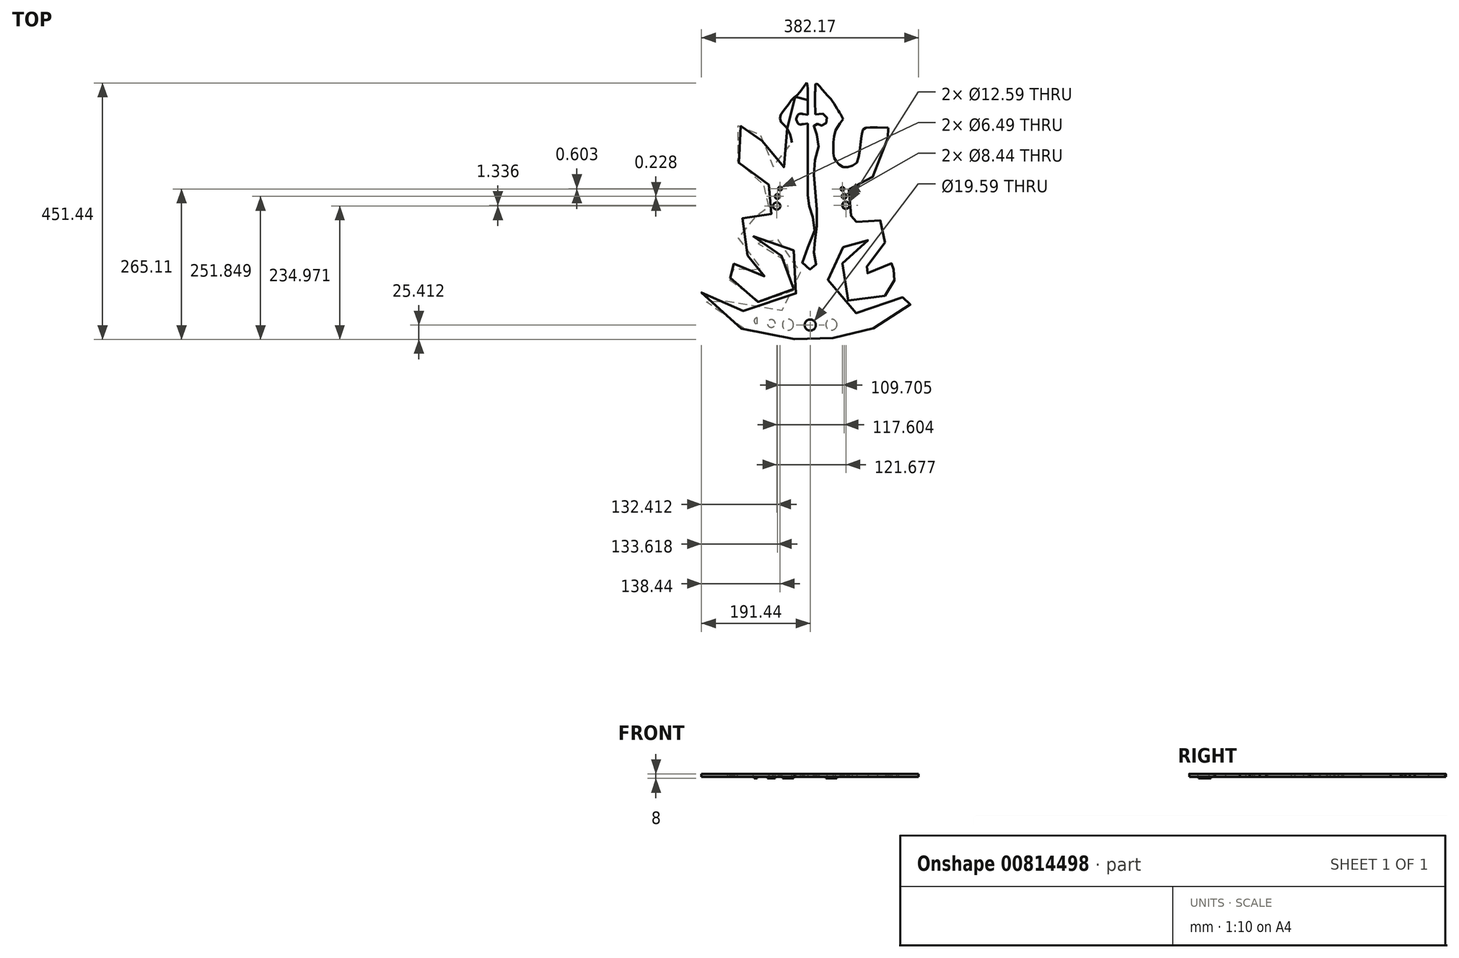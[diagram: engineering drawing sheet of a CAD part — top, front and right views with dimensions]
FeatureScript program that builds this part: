
annotation { "Feature Type Name" : "Feature", "Feature Type Description" : "" }
export const myFeature = defineFeature(function(context is Context, id is Id, definition is map)
    precondition{}
    {
        {
            var Q0;
            Q0=qCreatedBy(makeId("Top.planeOp"),FACE);
            var sketch = newSketch(context, id + "F0", { "sketchPlane" : qUnion([Q0])});
            skLineSegment(sketch, "E0", {"start": v(-4.07, 197.26) * mm, "end": v(-4.07, 171.34) * mm});
            skLineSegment(sketch, "E1", {"start": v(-4.07, 171.34) * mm, "end": v(-12.14, 172.64) * mm});
            skFitSpline(sketch, "E2", {"points": [v(-27.78, -223.43) * mm, v(-42.94, -221.77) * mm, v(-69.34, -218.88) * mm, v(-104.97, -210.79) * mm, v(-135.5, -198.39) * mm, v(-162.45, -178.55) * mm, v(-179.85, -161.54) * mm, v(-191.21, -140.43) * mm, v(-181.78, -135.12) * mm, v(-173.9, -139.63) * mm, v(-153.47, -153.55) * mm, v(-119.58, -173.02) * mm, v(-72.5, -180.75) * mm, v(-39.69, -165.64) * mm, v(-25.84, -144.71) * mm, v(-19.36, -127) * mm, v(-17.26, -107.43) * mm, v(-18.85, -88.24) * mm, v(-26.88, -70.7) * mm, v(-42.32, -56.3) * mm, v(-63.48, -45.68) * mm, v(-80.48, -39.04) * mm, v(-99.52, -40.32) * mm, v(-97.55, -50) * mm, v(-92.42, -54.8) * mm, v(-83.47, -58.4) * mm, v(-71.63, -62.83) * mm, v(-59.15, -70.9) * mm, v(-46.77, -80.5) * mm, v(-37.64, -92.94) * mm, v(-30.85, -106.86) * mm, v(-28.35, -119.67) * mm, v(-27.45, -129.59) * mm, v(-29.76, -137.09) * mm, v(-35.9, -144.2) * mm, v(-45.6, -151.88) * mm, v(-59.67, -157.06) * mm, v(-80.04, -159.95) * mm, v(-105.82, -152.76) * mm, v(-128.56, -141.2) * mm, v(-144.7, -127.23) * mm, v(-143.77, -118.69) * mm, v(-142.48, -116.34) * mm, v(-140.4, -115.67) * mm, v(-138.04, -115.96) * mm, v(-137.78, -113.15) * mm, v(-139.93, -110.3) * mm, v(-141.37, -105.83) * mm, v(-140.18, -100.45) * mm, v(-136.5, -99.2) * mm, v(-133.43, -99.09) * mm, v(-132.67, -96.28) * mm, v(-133.67, -92.96) * mm, v(-134.96, -86.24) * mm, v(-125.27, -87.3) * mm, v(-116.17, -95.98) * mm, v(-98.06, -103.5) * mm, v(-87, -112.38) * mm, v(-71.72, -109.66) * mm, v(-75.02, -105.8) * mm, v(-77.34, -103.91) * mm, v(-84.68, -99.95) * mm, v(-96.09, -91.59) * mm, v(-109.3, -77.45) * mm, v(-120.5, -61.9) * mm, v(-126.28, -45.64) * mm, v(-128.12, -31.2) * mm, v(-126.19, -17.15) * mm, v(-113.92, -8.45) * mm, v(-97.91, -6.5) * mm, v(-83.24, -8) * mm, v(-72.65, -14.15) * mm, v(-65.12, -8.82) * mm, v(-70.22, -0.24) * mm, v(-72.66, 8.71) * mm, v(-72.74, 20.19) * mm, v(-69.7, 30.44) * mm, v(-66.22, 39.17) * mm, v(-69.23, 47.47) * mm, v(-78.48, 47.54) * mm, v(-88.89, 50.35) * mm, v(-100.81, 57) * mm, v(-113.16, 67.16) * mm, v(-123.18, 81.99) * mm, v(-131.46, 100.93) * mm, v(-134, 120.7) * mm, v(-139.55, 138.3) * mm, v(-128.76, 152.03) * mm, v(-114.95, 149.55) * mm, v(-103.32, 150.04) * mm, v(-96.62, 149.3) * mm, v(-90.65, 148.51) * mm, v(-89.41, 141.65) * mm, v(-86.78, 133.64) * mm, v(-83.73, 118.01) * mm, v(-80.5, 101.92) * mm, v(-74.75, 85.75) * mm, v(-62.71, 79.55) * mm, v(-48.22, 78.44) * mm, v(-35.8, 91.84) * mm, v(-32.91, 108.6) * mm, v(-32.69, 125.44) * mm, v(-37.13, 140.3) * mm, v(-44.1, 152.06) * mm, v(-52.65, 161.04) * mm, v(-51.16, 173.08) * mm, v(-42.39, 184.23) * mm, v(-30.13, 200.74) * mm, v(-19.64, 208.94) * mm, v(-6.48, 227.3) * mm, v(-4.56, 217.3) * mm, v(-4.29, 209.32) * mm, v(-4.15, 201.7) * mm, v(-4.07, 197.26) * mm]});
            skLineSegment(sketch, "E3", {"start": v(-12.14, 155.2) * mm, "end": v(-4.07, 156.51) * mm});
            skLineSegment(sketch, "E4", {"start": v(-4.07, 156.51) * mm, "end": v(-4.07, 30.08) * mm});
            skFitSpline(sketch, "E5", {"points": [v(-12.14, 172.64) * mm, v(-13.86, 172.95) * mm, v(-16.72, 173.45) * mm, v(-20.98, 172.24) * mm, v(-22.95, 168.98) * mm, v(-24.42, 165.75) * mm, v(-24.42, 162.1) * mm, v(-22.95, 158.87) * mm, v(-20.98, 155.6) * mm, v(-16.72, 154.4) * mm, v(-13.86, 154.9) * mm, v(-12.14, 155.2) * mm]});
            skLineSegment(sketch, "E6", {"start": v(15.66, 173) * mm, "end": v(9.05, 172.22) * mm});
            skLineSegment(sketch, "E7", {"start": v(9.05, 172.22) * mm, "end": v(8.5, 196.44) * mm});
            skFitSpline(sketch, "E8", {"points": [v(-4.07, 30.08) * mm, v(0.64, 2.36) * mm, v(7.04, -35.24) * mm, v(-12.93, -93.82) * mm, v(8.43, -98.54) * mm, v(6.9, -73.98) * mm, v(10.46, -38.3) * mm, v(10.12, 24.62) * mm, v(7.47, 86.7) * mm, v(14.74, 126.78) * mm, v(6.06, 150.58) * mm, v(10.96, 156.05) * mm, v(12.9, 155.35) * mm, v(16, 153.85) * mm, v(21.44, 152.49) * mm, v(27.59, 156.03) * mm, v(29.76, 162.49) * mm, v(28.16, 168.96) * mm, v(22.57, 173.23) * mm, v(18.1, 173.08) * mm, v(15.66, 173) * mm]});
            skLineSegment(sketch, "E9", {"start": v(53.13, 172.82) * mm, "end": v(57.73, 163.81) * mm});
            skLineSegment(sketch, "E10", {"start": v(57.73, 163.81) * mm, "end": v(51.96, 156.16) * mm});
            skFitSpline(sketch, "E11", {"points": [v(8.5, 196.44) * mm, v(8.48, 200.64) * mm, v(8.43, 207.95) * mm, v(8.72, 215.84) * mm, v(10.22, 226.22) * mm, v(27.3, 208.98) * mm, v(38.21, 196.83) * mm, v(48.1, 180.91) * mm, v(53.13, 172.82) * mm]});
            skLineSegment(sketch, "E12", {"start": v(118, 149.2) * mm, "end": v(137, 148.51) * mm});
            skLineSegment(sketch, "E13", {"start": v(137, 148.51) * mm, "end": v(136.6, 130.73) * mm});
            skFitSpline(sketch, "E14", {"points": [v(51.96, 156.16) * mm, v(49.65, 152.5) * mm, v(44.74, 144.7) * mm, v(41.51, 129.6) * mm, v(40.88, 115.06) * mm, v(41.03, 103) * mm, v(42.36, 94.86) * mm, v(46.59, 88.17) * mm, v(52.62, 82.2) * mm, v(61.87, 79.03) * mm, v(71.4, 80.56) * mm, v(81.27, 86.3) * mm, v(86.1, 101.43) * mm, v(87.95, 117.39) * mm, v(89.9, 132.44) * mm, v(91.71, 141.38) * mm, v(94.53, 147.33) * mm, v(100.44, 148.82) * mm, v(108.05, 149.43) * mm, v(114.31, 149.28) * mm, v(118, 149.2) * mm]});
            skLineSegment(sketch, "E15", {"start": v(-27.78, -223.43) * mm, "end": v(-27.78, -223.43) * mm});
            skFitSpline(sketch, "E16", {"points": [v(136.6, 130.73) * mm, v(134.72, 117.75) * mm, v(131.09, 92.65) * mm, v(109.62, 61.76) * mm, v(86.9, 50.24) * mm, v(73.37, 47.56) * mm, v(70.04, 46.2) * mm, v(67.28, 44.07) * mm, v(67.98, 39.93) * mm, v(68.66, 34.92) * mm, v(71.23, 25.92) * mm, v(74.1, 14.75) * mm, v(74.04, 0.98) * mm, v(70.44, -8.65) * mm, v(67.55, -15.7) * mm, v(66.47, -19.1) * mm, v(66.49, -22.73) * mm, v(70.32, -21.7) * mm, v(73.97, -20.63) * mm, v(79.68, -17.9) * mm, v(86.79, -15.27) * mm, v(95.24, -13.2) * mm, v(104.7, -12) * mm, v(113.21, -11) * mm, v(121.49, -12.96) * mm, v(126.38, -18.58) * mm, v(132.04, -23.5) * mm, v(133.96, -31.95) * mm, v(132.86, -40.83) * mm, v(131.83, -50.54) * mm, v(129.4, -59.13) * mm, v(124.8, -68.94) * mm, v(115.72, -79.87) * mm, v(103.93, -92.1) * mm, v(93.6, -100.17) * mm, v(86.96, -104.93) * mm, v(84.8, -106.96) * mm, v(82.54, -110.6) * mm, v(93.53, -111.43) * mm, v(102.94, -106.41) * mm, v(117.74, -100.94) * mm, v(129.33, -94.52) * mm, v(136.23, -92.35) * mm, v(140.93, -88.8) * mm, v(143.94, -92.13) * mm, v(141.44, -96.46) * mm, v(138.85, -100.35) * mm, v(133.29, -104.15) * mm, v(137.44, -108.85) * mm, v(142.5, -104.71) * mm, v(148.88, -100.28) * mm, v(152.53, -107.9) * mm, v(146.96, -113.72) * mm, v(141.76, -117.65) * mm, v(142.21, -124.34) * mm, v(147.9, -120.35) * mm, v(152.15, -117.65) * mm, v(155.87, -122) * mm, v(152.5, -129.64) * mm, v(144.33, -138.59) * mm, v(130.25, -147.93) * mm, v(111.68, -156.34) * mm, v(90.6, -159.74) * mm, v(69.55, -156.71) * mm, v(50.9, -144.4) * mm, v(45, -118.03) * mm, v(57.52, -89.31) * mm, v(78.11, -70.27) * mm, v(93.37, -59.83) * mm, v(101.85, -53.6) * mm, v(100.28, -46.98) * mm, v(94.27, -44.13) * mm, v(85.45, -46.21) * mm, v(73.7, -51.09) * mm, v(59.8, -59.9) * mm, v(47, -71.52) * mm, v(34.4, -87.22) * mm, v(30.25, -110.58) * mm, v(35.13, -136.65) * mm, v(50.44, -162.28) * mm, v(81.3, -177.61) * mm, v(121.17, -173.42) * mm, v(153.55, -155.2) * mm, v(172.05, -143.18) * mm, v(185.83, -135.03) * mm, v(190.31, -148.68) * mm, v(175.16, -163.56) * mm, v(156.15, -182.25) * mm, v(130.34, -197.3) * mm, v(104.67, -206.44) * mm, v(81.91, -213.55) * mm, v(57.48, -219.65) * mm, v(29.45, -222.08) * mm, v(0.4, -224.1) * mm, v(-19.38, -223.63) * mm, v(-27.78, -223.43) * mm]});
            skSolve(sketch);
        }
        {
            var Q0;
            Q0=makeQuery(id+"F0.imprint","IMPRINT",FACE,{"disambiguationData":[TD([[makeQuery(id+"F0.imprint","IMPRINT",EDGE,{"derivedFrom":sQuery(id+"F0.wireOp",EDGE,"E0")}),-1.0]])]});
            var sketch = newSketch(context, id + "F1", { "sketchPlane" : qUnion([Q0])});
            skSolve(sketch);
        }
        {
            var Q0;
            Q0=makeQuery(id+"F1.imprint","IMPRINT",FACE,{"disambiguationData":[TD([[makeQuery(id+"F1.imprint","IMPRINT",EDGE,{"derivedFrom":makeQuery(id+"F0.imprint","IMPRINT",EDGE,{"derivedFrom":sQuery(id+"F0.wireOp",EDGE,"E0")})}),-1.0]])]});
            extrude(context, id + "F2", {"entities" : qUnion([Q0]), "depth" : 5 * mm, "offsetDistance" : 25 * mm});
        }
        {
            var Q0;
            Q0=makeQuery(id+"F2.opExtrude","CAP_FACE",FACE,{"disambiguationData":[OSD([sQuery(id+"F0.wireOp",EDGE,"E0"),sQuery(id+"F0.wireOp",EDGE,"E1"),sQuery(id+"F0.wireOp",EDGE,"E2"),sQuery(id+"F0.wireOp",EDGE,"E3"),sQuery(id+"F0.wireOp",EDGE,"E4"),sQuery(id+"F0.wireOp",EDGE,"E5"),sQuery(id+"F0.wireOp",EDGE,"E6"),sQuery(id+"F0.wireOp",EDGE,"E7"),sQuery(id+"F0.wireOp",EDGE,"E8"),sQuery(id+"F0.wireOp",EDGE,"E9"),sQuery(id+"F0.wireOp",EDGE,"E10"),sQuery(id+"F0.wireOp",EDGE,"E11"),sQuery(id+"F0.wireOp",EDGE,"E12"),sQuery(id+"F0.wireOp",EDGE,"E13"),sQuery(id+"F0.wireOp",EDGE,"E14"),sQuery(id+"F0.wireOp",EDGE,"E15"),sQuery(id+"F0.wireOp",EDGE,"E16")])],"isStart":false});
            var sketch = newSketch(context, id + "F3", { "sketchPlane" : qUnion([Q0])});
            skCircle(sketch, "E17", {"center": v(0, -198.73) * mm, "radius": 9.8 * mm});
            skSolve(sketch);
        }
        {
            var Q0;
            Q0 = qSketchRegion(id + "F3", true);
            var Q1;
            Q1 = qSketchRegion(id + "F5", true);
            extrude(context, id + "F4", {"entities" : qUnion([Q0, Q1]), "operationType" : NewBodyOperationType.REMOVE, "oppositeDirection" : true, "depth" : 25 * mm, "offsetDistance" : 25 * mm});
        }
        {
            var Q0;
            Q0=makeQuery(id+"F0.imprint","IMPRINT",FACE,{"disambiguationData":[TD([[makeQuery(id+"F0.imprint","IMPRINT",EDGE,{"derivedFrom":sQuery(id+"F0.wireOp",EDGE,"E0")}),-1.0]])]});
            var sketch = newSketch(context, id + "F5", { "sketchPlane" : qUnion([Q0])});
            skCircle(sketch, "E18", {"center": v(-59.03, 10.83) * mm, "radius": 6.3 * mm});
            skCircle(sketch, "E19", {"center": v(-57.82, 27.7) * mm, "radius": 4.22 * mm});
            skCircle(sketch, "E20", {"center": v(-53, 41.57) * mm, "radius": 3.25 * mm});
            skCircle(sketch, "E21", {"center": v(62.65, 12.17) * mm, "radius": 6.3 * mm});
            skCircle(sketch, "E22", {"center": v(59.78, 27.94) * mm, "radius": 4.22 * mm});
            skCircle(sketch, "E23", {"center": v(56.7, 40.97) * mm, "radius": 3.25 * mm});
            skSolve(sketch);
        }
        {
            var Q0;
            Q0=makeQuery(id+"F5.imprint","IMPRINT",FACE,{"disambiguationData":[TD([[makeQuery(id+"F5.imprint","IMPRINT",EDGE,{"derivedFrom":sQuery(id+"F5.wireOp",EDGE,"E21")}),1.0]])]});
            var Q1;
            Q1=makeQuery(id+"F5.imprint","IMPRINT",FACE,{"disambiguationData":[TD([[makeQuery(id+"F5.imprint","IMPRINT",EDGE,{"derivedFrom":sQuery(id+"F5.wireOp",EDGE,"E18")}),1.0]])]});
            var Q2;
            Q2=makeQuery(id+"F5.imprint","IMPRINT",FACE,{"disambiguationData":[TD([[makeQuery(id+"F5.imprint","IMPRINT",EDGE,{"derivedFrom":sQuery(id+"F5.wireOp",EDGE,"E20")}),1.0]])]});
            var Q3;
            Q3=makeQuery(id+"F5.imprint","IMPRINT",FACE,{"disambiguationData":[TD([[makeQuery(id+"F5.imprint","IMPRINT",EDGE,{"derivedFrom":sQuery(id+"F5.wireOp",EDGE,"E22")}),1.0]])]});
            var Q4;
            Q4=makeQuery(id+"F5.imprint","IMPRINT",FACE,{"disambiguationData":[TD([[makeQuery(id+"F5.imprint","IMPRINT",EDGE,{"derivedFrom":sQuery(id+"F5.wireOp",EDGE,"E19")}),1.0]])]});
            var Q5;
            Q5=makeQuery(id+"F5.imprint","IMPRINT",FACE,{"disambiguationData":[TD([[makeQuery(id+"F5.imprint","IMPRINT",EDGE,{"derivedFrom":sQuery(id+"F5.wireOp",EDGE,"E23")}),1.0]])]});
            extrude(context, id + "F6", {"entities" : qUnion([Q0, Q1, Q2, Q3, Q4, Q5]), "operationType" : NewBodyOperationType.REMOVE, "depth" : 5 * mm, "offsetDistance" : 25 * mm});
        }
        {
            var Q0;
            Q0=makeQuery(id+"F0.imprint","IMPRINT",FACE,{"disambiguationData":[TD([[makeQuery(id+"F0.imprint","IMPRINT",EDGE,{"derivedFrom":sQuery(id+"F0.wireOp",EDGE,"E0")}),-1.0]])]});
            var sketch = newSketch(context, id + "F7", { "sketchPlane" : qUnion([Q0])});
            skCircle(sketch, "E24", {"center": v(37.2, -198.04) * mm, "radius": 9.8 * mm});
            skCircle(sketch, "E25", {"center": v(69.49, -195.54) * mm, "radius": 6.87 * mm});
            skCircle(sketch, "E26", {"center": v(92.8, -191.49) * mm, "radius": 5.46 * mm});
            skCircle(sketch, "E27", {"center": v(-39.23, -198.15) * mm, "radius": 9.8 * mm});
            skCircle(sketch, "E28", {"center": v(-68.38, -196.05) * mm, "radius": 6.87 * mm});
            skCircle(sketch, "E29", {"center": v(-93.22, -191.49) * mm, "radius": 5.46 * mm});
            skLineSegment(sketch, "E30", {"start": v(-93.22, -196.95) * mm, "end": v(-93.22, -186.03) * mm});
            skSolve(sketch);
        }
        {
            var Q0;
            Q0=makeQuery(id+"F7.imprint","IMPRINT",FACE,{"disambiguationData":[TD([[makeQuery(id+"F7.imprint","IMPRINT",EDGE,{"derivedFrom":sQuery(id+"F7.wireOp",EDGE,"E28")}),1.0]])]});
            var Q1;
            Q1=makeQuery(id+"F7.imprint","IMPRINT",FACE,{"disambiguationData":[TD([[makeQuery(id+"F7.imprint","IMPRINT",EDGE,{"derivedFrom":sQuery(id+"F7.wireOp",EDGE,"E27")}),1.0]])]});
            var Q2;
            {var subQ0=sQuery(id+"F7.wireOp",EDGE,"E30");Q2=makeQuery(id+"F7.imprint","IMPRINT",FACE,{"disambiguationData":[TD([[makeQuery(id+"F7.imprint","IMPRINT",EDGE,{"derivedFrom":subQ0}),1.0]])]});}
            var Q3;
            Q3=makeQuery(id+"F7.imprint","IMPRINT",FACE,{"disambiguationData":[TD([[makeQuery(id+"F7.imprint","IMPRINT",EDGE,{"derivedFrom":sQuery(id+"F7.wireOp",EDGE,"E24")}),1.0]])]});
            extrude(context, id + "F8", {"entities" : qUnion([Q0, Q1, Q2, Q3]), "operationType" : NewBodyOperationType.ADD, "oppositeDirection" : true, "depth" : 3 * mm, "offsetDistance" : 25 * mm});
        }
    });
